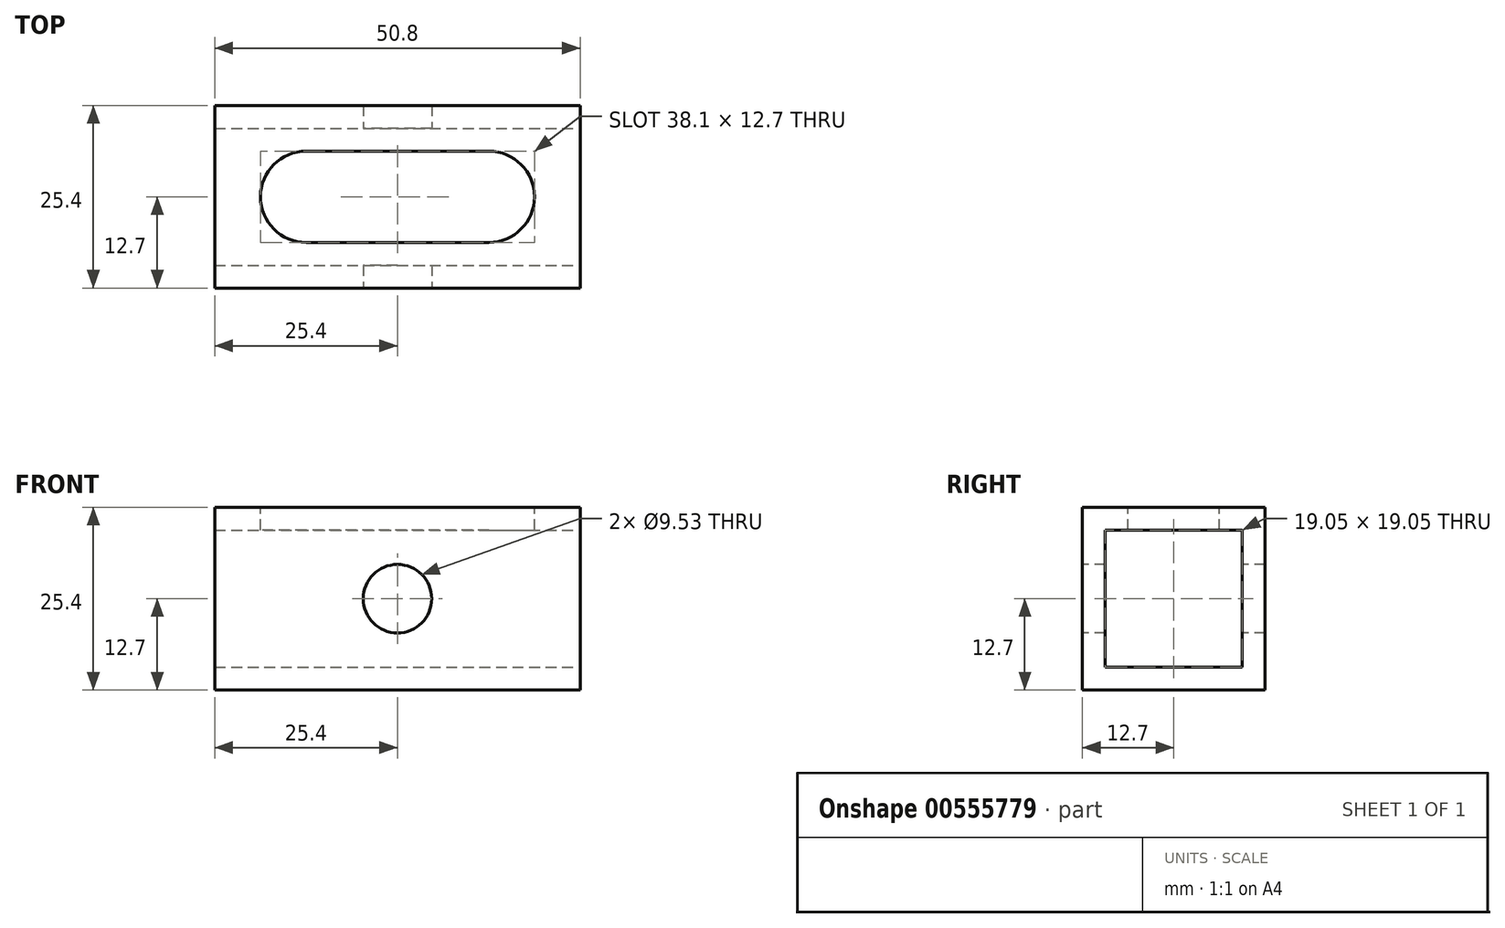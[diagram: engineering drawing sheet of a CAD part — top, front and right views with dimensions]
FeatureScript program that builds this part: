
annotation { "Feature Type Name" : "Feature", "Feature Type Description" : "" }
export const myFeature = defineFeature(function(context is Context, id is Id, definition is map)
    precondition{}
    {
        {
            var Q0;
            Q0=qCreatedBy(makeId("Top.planeOp"),FACE);
            var sketch = newSketch(context, id + "F0", { "sketchPlane" : qUnion([Q0])});
            skLineSegment(sketch, "E0.bottom", {"start": v(0, 0) * mm, "end": v(50.8, 0) * mm});
            skLineSegment(sketch, "E0.top", {"start": v(0, 25.4) * mm, "end": v(50.8, 25.4) * mm});
            skLineSegment(sketch, "E0.left", {"start": v(0, 0) * mm, "end": v(0, 25.4) * mm});
            skLineSegment(sketch, "E0.right", {"start": v(50.8, 0) * mm, "end": v(50.8, 25.4) * mm});
            skSolve(sketch);
        }
        {
            var Q0;
            Q0=makeQuery(id+"F0.imprint","IMPRINT",FACE,{"disambiguationData":[TD([[makeQuery(id+"F0.imprint","IMPRINT",EDGE,{"derivedFrom":sQuery(id+"F0.wireOp",EDGE,"E0.bottom")}),1.0]])]});
            extrude(context, id + "F1", {"entities" : qUnion([Q0]), "depth" : 25.4 * mm, "offsetDistance" : 25.4 * mm});
        }
        {
            var Q0;
            Q0=makeQuery(id+"F1.opExtrude","SWEPT_FACE",FACE,{"disambiguationData":[OSD([sQuery(id+"F0.wireOp",EDGE,"E0.right")])]});
            var sketch = newSketch(context, id + "F2", { "sketchPlane" : qUnion([Q0])});
            skLineSegment(sketch, "E1.bottom", {"start": v(0, 0) * mm, "end": v(25.4, 0) * mm});
            skLineSegment(sketch, "E1.top", {"start": v(0, 25.4) * mm, "end": v(25.4, 25.4) * mm});
            skLineSegment(sketch, "E1.left", {"start": v(0, 0) * mm, "end": v(0, 25.4) * mm});
            skLineSegment(sketch, "E1.right", {"start": v(25.4, 0) * mm, "end": v(25.4, 25.4) * mm});
            skLineSegment(sketch, "E2.0", {"start": v(3.17, 3.17) * mm, "end": v(3.17, 22.23) * mm});
            skLineSegment(sketch, "E2.1", {"start": v(3.17, 3.17) * mm, "end": v(22.22, 3.17) * mm});
            skLineSegment(sketch, "E2.2", {"start": v(22.22, 3.17) * mm, "end": v(22.22, 22.23) * mm});
            skLineSegment(sketch, "E2.3", {"start": v(3.17, 22.23) * mm, "end": v(22.22, 22.23) * mm});
            skSolve(sketch);
        }
        {
            var Q0;
            Q0=makeQuery(id+"F2.imprint","IMPRINT",FACE,{"disambiguationData":[TD([[makeQuery(id+"F2.imprint","IMPRINT",EDGE,{"derivedFrom":sQuery(id+"F2.wireOp",EDGE,"E2.0")}),-1.0]])]});
            extrude(context, id + "F3", {"entities" : qUnion([Q0]), "operationType" : NewBodyOperationType.REMOVE, "endBound" : BoundingType.THROUGH_ALL, "oppositeDirection" : true, "depth" : 25.4 * mm, "offsetDistance" : 25.4 * mm});
        }
        {
            var Q0;
            Q0=makeQuery(id+"F1.opExtrude","SWEPT_FACE",FACE,{"disambiguationData":[OSD([sQuery(id+"F0.wireOp",EDGE,"E0.bottom")])]});
            var sketch = newSketch(context, id + "F4", { "sketchPlane" : qUnion([Q0])});
            skCircle(sketch, "E3", {"center": v(25.4, 12.7) * mm, "radius": 4.76 * mm});
            skSolve(sketch);
        }
        {
            var Q0;
            Q0=makeQuery(id+"F4.imprint","IMPRINT",FACE,{"disambiguationData":[TD([[makeQuery(id+"F4.imprint","IMPRINT",EDGE,{"derivedFrom":sQuery(id+"F4.wireOp",EDGE,"E3")}),1.0]])]});
            extrude(context, id + "F5", {"entities" : qUnion([Q0]), "operationType" : NewBodyOperationType.REMOVE, "endBound" : BoundingType.THROUGH_ALL, "oppositeDirection" : true, "depth" : 25.4 * mm, "offsetDistance" : 25.4 * mm});
        }
        {
            var Q0;
            Q0=makeQuery(id+"F1.opExtrude","CAP_FACE",FACE,{"disambiguationData":[OSD([sQuery(id+"F0.wireOp",EDGE,"E0.bottom"),sQuery(id+"F0.wireOp",EDGE,"E0.top"),sQuery(id+"F0.wireOp",EDGE,"E0.left"),sQuery(id+"F0.wireOp",EDGE,"E0.right")])],"isStart":false});
            var sketch = newSketch(context, id + "F6", { "sketchPlane" : qUnion([Q0])});
            skLineSegment(sketch, "E4.bottom", {"start": v(38.1, 6.35) * mm, "end": v(12.7, 6.35) * mm});
            skLineSegment(sketch, "E4.top", {"start": v(38.1, 19.05) * mm, "end": v(12.7, 19.05) * mm});
            skLineSegment(sketch, "E4.left", {"start": v(38.1, 6.35) * mm, "end": v(38.1, 19.05) * mm});
            skLineSegment(sketch, "E4.right", {"start": v(12.7, 6.35) * mm, "end": v(12.7, 19.05) * mm});
            skPoint(sketch, "E4.middle", {"position": v(25.4, 12.7) * mm});
            skCircle(sketch, "E5", {"center": v(12.7, 12.7) * mm, "radius": 6.35 * mm});
            skCircle(sketch, "E6", {"center": v(38.1, 12.7) * mm, "radius": 6.35 * mm});
            skSolve(sketch);
        }
        {
            var Q0;
            {var subQ0=sQuery(id+"F6.wireOp",EDGE,"E4.right");Q0=makeQuery(id+"F6.imprint","IMPRINT",FACE,{"disambiguationData":[TD([[makeQuery(id+"F6.imprint","IMPRINT",EDGE,{"derivedFrom":subQ0}),1.0]])]});}
            var Q1;
            {var subQ0=sQuery(id+"F6.wireOp",EDGE,"E4.right");Q1=makeQuery(id+"F6.imprint","IMPRINT",FACE,{"disambiguationData":[TD([[makeQuery(id+"F6.imprint","IMPRINT",EDGE,{"derivedFrom":subQ0}),-1.0]])]});}
            var Q2;
            {var subQ0=sQuery(id+"F6.wireOp",EDGE,"E4.bottom");Q2=makeQuery(id+"F6.imprint","IMPRINT",FACE,{"disambiguationData":[TD([[makeQuery(id+"F6.imprint","IMPRINT",EDGE,{"derivedFrom":subQ0}),-1.0]])]});}
            var Q3;
            {var subQ0=sQuery(id+"F6.wireOp",EDGE,"E4.left");Q3=makeQuery(id+"F6.imprint","IMPRINT",FACE,{"disambiguationData":[TD([[makeQuery(id+"F6.imprint","IMPRINT",EDGE,{"derivedFrom":subQ0}),1.0]])]});}
            var Q4;
            {var subQ0=sQuery(id+"F6.wireOp",EDGE,"E4.left");Q4=makeQuery(id+"F6.imprint","IMPRINT",FACE,{"disambiguationData":[TD([[makeQuery(id+"F6.imprint","IMPRINT",EDGE,{"derivedFrom":subQ0}),-1.0]])]});}
            extrude(context, id + "F7", {"entities" : qUnion([Q0, Q1, Q2, Q3, Q4]), "operationType" : NewBodyOperationType.REMOVE, "endBound" : BoundingType.UP_TO_NEXT, "oppositeDirection" : true, "depth" : 25.4 * mm, "offsetDistance" : 25.4 * mm});
        }
    });
